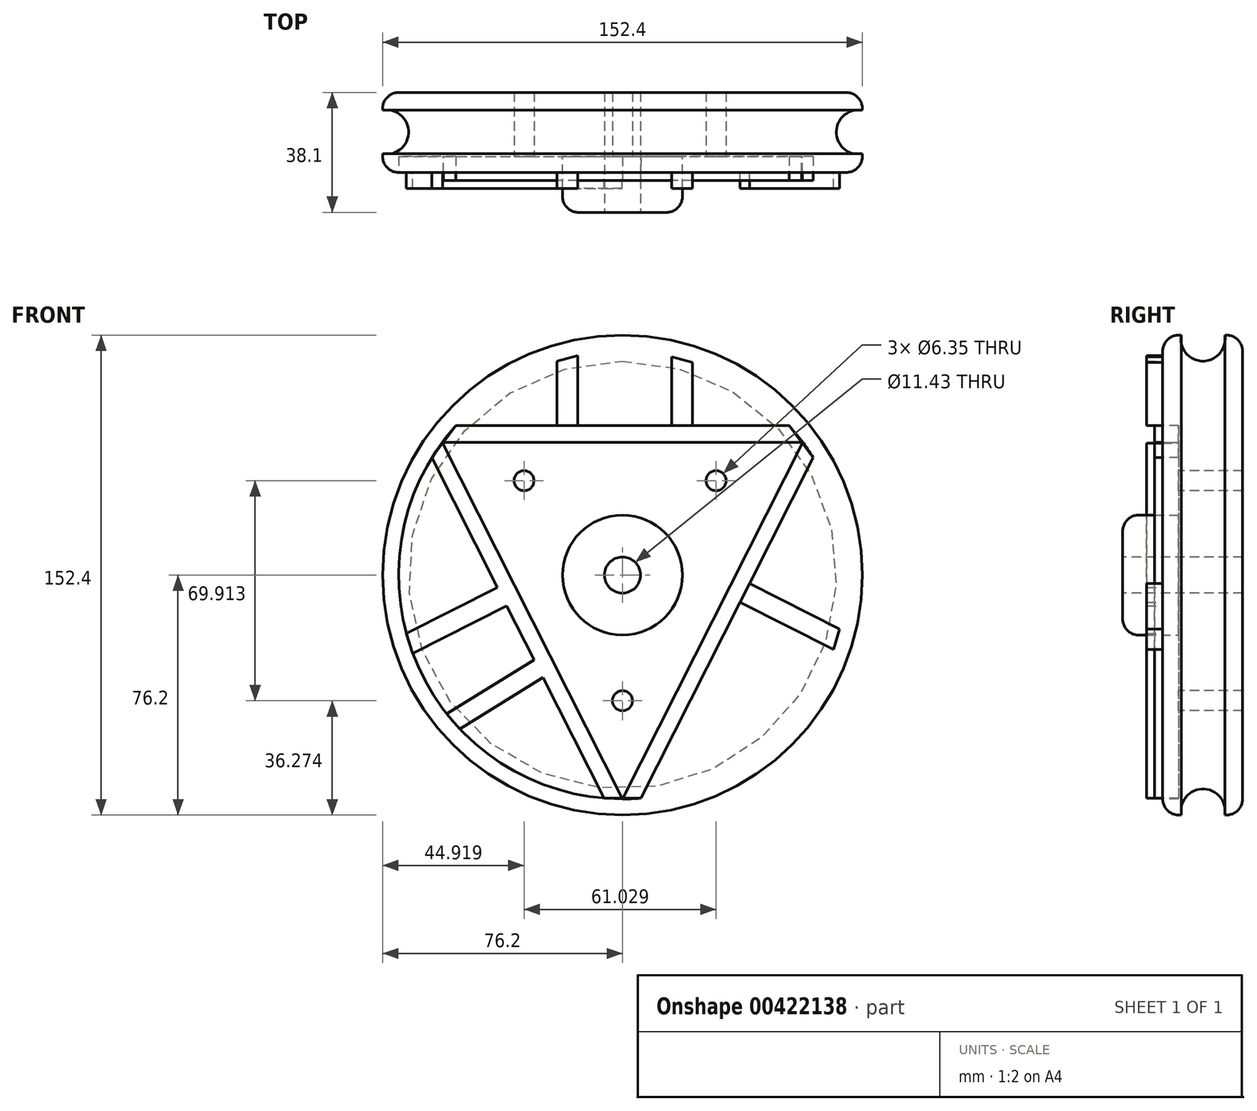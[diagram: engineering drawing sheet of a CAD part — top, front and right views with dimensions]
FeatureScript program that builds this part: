
annotation { "Feature Type Name" : "Feature", "Feature Type Description" : "" }
export const myFeature = defineFeature(function(context is Context, id is Id, definition is map)
    precondition{}
    {
        {
            var Q0;
            Q0=qCreatedBy(makeId("Front.planeOp"),FACE);
            var sketch = newSketch(context, id + "F0", { "sketchPlane" : qUnion([Q0])});
            skCircle(sketch, "E0", {"center": v(0, 0) * mm, "radius": 76.2 * mm});
            skSolve(sketch);
        }
        {
            var Q0;
            Q0=makeQuery(id+"F0.imprint","IMPRINT",FACE,{"disambiguationData":[TD([[makeQuery(id+"F0.imprint","IMPRINT",EDGE,{"derivedFrom":sQuery(id+"F0.wireOp",EDGE,"E0")}),1.0]])]});
            extrude(context, id + "F1", {"entities" : qUnion([Q0]), "depth" : 25.4 * mm, "offsetDistance" : 25.4 * mm});
        }
        {
            var Q0;
            Q0=makeQuery(id+"F1.opExtrude","CAP_FACE",FACE,{"disambiguationData":[OSD([sQuery(id+"F0.wireOp",EDGE,"E0")])],"isStart":false});
            var sketch = newSketch(context, id + "F2", { "sketchPlane" : qUnion([Q0])});
            skCircle(sketch, "E1", {"center": v(0, 0) * mm, "radius": 19.05 * mm});
            skSolve(sketch);
        }
        {
            var Q0;
            Q0=makeQuery(id+"F2.imprint","IMPRINT",FACE,{"disambiguationData":[TD([[makeQuery(id+"F2.imprint","IMPRINT",EDGE,{"derivedFrom":sQuery(id+"F2.wireOp",EDGE,"E1")}),1.0]])]});
            extrude(context, id + "F3", {"entities" : qUnion([Q0]), "operationType" : NewBodyOperationType.ADD, "depth" : 12.7 * mm, "offsetDistance" : 25.4 * mm});
        }
        {
            var Q0;
            Q0=makeQuery(id+"F1.opExtrude","CAP_EDGE",EDGE,{"disambiguationData":[OSD([sQuery(id+"F0.wireOp",EDGE,"E0")])],"isStart":false});
            var Q1;
            Q1=makeQuery(id+"F1.opExtrude","CAP_EDGE",EDGE,{"disambiguationData":[OSD([sQuery(id+"F0.wireOp",EDGE,"E0")])],"isStart":true});
            fillet(context, id + "F4", {"entities" : qUnion([Q0, Q1]), "radius" : 5.08 * mm, "tangentPropagation" : true, "allowEdgeOverflow" : false});
        }
        {
            var Q0;
            Q0=makeQuery(id+"F3.opExtrude","CAP_FACE",FACE,{"disambiguationData":[OSD([sQuery(id+"F2.wireOp",EDGE,"E1")])],"isStart":false});
            var sketch = newSketch(context, id + "F5", { "sketchPlane" : qUnion([Q0])});
            skCircle(sketch, "E2", {"center": v(0, 0) * mm, "radius": 5.72 * mm});
            skSolve(sketch);
        }
        {
            var Q0;
            Q0=makeQuery(id+"F5.imprint","IMPRINT",FACE,{"disambiguationData":[TD([[makeQuery(id+"F5.imprint","IMPRINT",EDGE,{"derivedFrom":sQuery(id+"F5.wireOp",EDGE,"E2")}),1.0]])]});
            extrude(context, id + "F6", {"entities" : qUnion([Q0]), "operationType" : NewBodyOperationType.REMOVE, "oppositeDirection" : true, "depth" : 76.2 * mm, "offsetDistance" : 25.4 * mm});
        }
        {
            var Q0;
            Q0=makeQuery(id+"F3.opExtrude","CAP_EDGE",EDGE,{"disambiguationData":[OSD([sQuery(id+"F2.wireOp",EDGE,"E1")])],"isStart":false});
            fillet(context, id + "F7", {"entities" : qUnion([Q0]), "radius" : 5.08 * mm, "tangentPropagation" : true, "allowEdgeOverflow" : false});
        }
        {
            var Q0;
            Q0=qCreatedBy(makeId("Right.planeOp"),FACE);
            var sketch = newSketch(context, id + "F8", { "sketchPlane" : qUnion([Q0])});
            skCircle(sketch, "E3", {"center": v(-12.58, 74.98) * mm, "radius": 7.03 * mm});
            skSolve(sketch);
        }
        {
            var Q0;
            Q0=makeQuery(id+"F8.imprint","IMPRINT",FACE,{"disambiguationData":[TD([[makeQuery(id+"F8.imprint","IMPRINT",EDGE,{"derivedFrom":sQuery(id+"F8.wireOp",EDGE,"E3")}),1.0]])]});
            var Q1;
            Q1=makeQuery(id+"F1.opExtrude","SWEPT_FACE",FACE,{"disambiguationData":[OSD([sQuery(id+"F0.wireOp",EDGE,"E0")])]});
            revolve(context, id + "F9", {"operationType" : NewBodyOperationType.REMOVE, "entities" : qUnion([Q0]), "axis" : qUnion([Q1]), "revolveType" : RevolveType.FULL, "oppositeDirection" : true});
        }
        {
            var Q0;
            Q0=makeQuery(id+"F1.opExtrude","CAP_FACE",FACE,{"disambiguationData":[OSD([sQuery(id+"F0.wireOp",EDGE,"E0")])],"isStart":false});
            var sketch = newSketch(context, id + "F10", { "sketchPlane" : qUnion([Q0])});
            skPoint(sketch, "E4", {"position": v(0, 44.32) * mm});
            skPoint(sketch, "E5", {"position": v(29.75, 29.99) * mm});
            skPoint(sketch, "E6", {"position": v(43.57, 0) * mm});
            skPoint(sketch, "E7", {"position": v(-31.28, 29.99) * mm});
            skPoint(sketch, "E8", {"position": v(-44.48, 0) * mm});
            skPoint(sketch, "E9", {"position": v(0, -39.93) * mm});
            skPoint(sketch, "E10", {"position": v(29.75, -26.1) * mm});
            skPoint(sketch, "E11", {"position": v(-31.28, -26.1) * mm});
            skSolve(sketch);
        }
        {
            var Q0;
            Q0=sQuery(id+"F10.wireOp",VERTEX,"E7");
            var Q1;
            Q1=sQuery(id+"F10.wireOp",VERTEX,"E9");
            var Q2;
            Q2=sQuery(id+"F10.wireOp",VERTEX,"E5");
            var Q3;
            Q3=makeQuery(id+"F1.opExtrude","SWEPT_BODY",BODY,{"disambiguationData":[OSD([sQuery(id+"F0.wireOp",EDGE,"E0")])]});
            hole(context, id + "F11", {"style" : HoleStyle.SIMPLE, "endStyle" : HoleEndStyle.THROUGH, "holeDiameter" : 6.35 * mm, "majorDiameter" : 6.35 * mm, "isTappedThrough" : true, "tappedDepth" : 12.7 * mm, "tapClearance" : 3, "locations" : qUnion([Q0, Q1, Q2]), "scope" : qUnion([Q3])});
        }
        {
            var Q0;
            Q0=makeQuery(id+"F1.opExtrude","CAP_FACE",FACE,{"disambiguationData":[OSD([sQuery(id+"F0.wireOp",EDGE,"E0")])],"isStart":false});
            var sketch = newSketch(context, id + "F12", { "sketchPlane" : qUnion([Q0])});
            skLineSegment(sketch, "E12", {"start": v(-57.28, 42.16) * mm, "end": v(57.28, 42.16) * mm});
            skLineSegment(sketch, "E13", {"start": v(57.28, 42.16) * mm, "end": v(0, -71.12) * mm});
            skLineSegment(sketch, "E14", {"start": v(0, -71.12) * mm, "end": v(-57.28, 42.16) * mm});
            skLineSegment(sketch, "E15", {"start": v(-60.57, 37.27) * mm, "end": v(-5.89, -70.88) * mm});
            skLineSegment(sketch, "E16", {"start": v(-5.89, -70.88) * mm, "end": v(5.89, -70.88) * mm});
            skLineSegment(sketch, "E17", {"start": v(5.89, -70.88) * mm, "end": v(60.57, 37.27) * mm});
            skLineSegment(sketch, "E18", {"start": v(60.57, 37.27) * mm, "end": v(52.98, 47.44) * mm});
            skLineSegment(sketch, "E19", {"start": v(52.98, 47.44) * mm, "end": v(-52.98, 47.44) * mm});
            skLineSegment(sketch, "E20", {"start": v(-52.98, 47.44) * mm, "end": v(-60.57, 37.27) * mm});
            skLineSegment(sketch, "E21", {"start": v(-36.76, -9.82) * mm, "end": v(-66.61, -24.9) * mm});
            skLineSegment(sketch, "E22", {"start": v(-66.61, -24.9) * mm, "end": v(-68.67, -18.5) * mm});
            skLineSegment(sketch, "E23", {"start": v(-68.67, -18.5) * mm, "end": v(-39.76, -3.89) * mm});
            skLineSegment(sketch, "E24", {"start": v(-39.76, -3.89) * mm, "end": v(-36.76, -9.82) * mm});
            skLineSegment(sketch, "E25", {"start": v(-25.26, -32.55) * mm, "end": v(-51.69, -48.85) * mm});
            skPoint(sketch, "E25.endSnap0", {"position": v(-51.69, -17.36) * mm});
            skLineSegment(sketch, "E26", {"start": v(-51.69, -48.85) * mm, "end": v(-55.83, -44.06) * mm});
            skLineSegment(sketch, "E27", {"start": v(-55.83, -44.06) * mm, "end": v(-28.1, -26.96) * mm});
            skLineSegment(sketch, "E28", {"start": v(-28.1, -26.96) * mm, "end": v(-25.26, -32.55) * mm});
            skLineSegment(sketch, "E29", {"start": v(25.27, -32.55) * mm, "end": v(28.1, -26.97) * mm});
            skLineSegment(sketch, "E30", {"start": v(28.1, -26.97) * mm, "end": v(25.27, -32.55) * mm});
            skLineSegment(sketch, "E31", {"start": v(53.34, -47.04) * mm, "end": v(25.27, -32.55) * mm});
            skLineSegment(sketch, "E32", {"start": v(28.1, -26.97) * mm, "end": v(57.5, -41.84) * mm});
            skLineSegment(sketch, "E33", {"start": v(57.5, -41.84) * mm, "end": v(53.34, -47.04) * mm});
            skLineSegment(sketch, "E34", {"start": v(37.36, -8.63) * mm, "end": v(67.07, -23.65) * mm});
            skLineSegment(sketch, "E35", {"start": v(67.07, -23.65) * mm, "end": v(69.01, -17.18) * mm});
            skLineSegment(sketch, "E36", {"start": v(69.01, -17.18) * mm, "end": v(40.37, -2.7) * mm});
            skLineSegment(sketch, "E37", {"start": v(40.37, -2.7) * mm, "end": v(37.36, -8.63) * mm});
            skLineSegment(sketch, "E38", {"start": v(-20.87, 47.44) * mm, "end": v(-20.87, 68) * mm});
            skLineSegment(sketch, "E39", {"start": v(-20.87, 68) * mm, "end": v(-14.21, 69.69) * mm});
            skLineSegment(sketch, "E40", {"start": v(-14.21, 69.69) * mm, "end": v(-14.21, 47.44) * mm});
            skLineSegment(sketch, "E41", {"start": v(15.58, 47.44) * mm, "end": v(15.58, 69.4) * mm});
            skLineSegment(sketch, "E42", {"start": v(15.58, 69.4) * mm, "end": v(22.24, 67.55) * mm});
            skLineSegment(sketch, "E43", {"start": v(22.24, 67.55) * mm, "end": v(22.24, 47.44) * mm});
            skSolve(sketch);
        }
        {
            var Q0;
            {var subQ5=sQuery(id+"F12.wireOp",EDGE,"E17");Q0=makeQuery(id+"F12.imprint","IMPRINT",FACE,{"disambiguationData":[TD([[makeQuery(id+"F12.imprint","IMPRINT",EDGE,{"derivedFrom":subQ5}),1.0]])]});}
            var Q1;
            {var subQ6=sQuery(id+"F12.wireOp",EDGE,"E19");Q1=makeQuery(id+"F12.imprint","IMPRINT",FACE,{"disambiguationData":[TD([[makeQuery(id+"F12.imprint","IMPRINT",EDGE,{"derivedFrom":subQ6}),1.0]])]});}
            extrude(context, id + "F13", {"entities" : qUnion([Q0, Q1]), "operationType" : NewBodyOperationType.ADD, "depth" : 2.54 * mm, "offsetDistance" : 25.4 * mm});
        }
        {
            var Q0;
            {var subQ5=sQuery(id+"F12.wireOp",EDGE,"E15");Q0=makeQuery(id+"F12.imprint","IMPRINT",FACE,{"disambiguationData":[TD([[makeQuery(id+"F12.imprint","IMPRINT",EDGE,{"derivedFrom":subQ5}),1.0]])]});}
            var Q1;
            Q1=makeQuery(id+"F12.imprint","IMPRINT",FACE,{"disambiguationData":[TD([[makeQuery(id+"F12.imprint","IMPRINT",EDGE,{"derivedFrom":sQuery(id+"F12.wireOp",EDGE,"E21")}),-1.0]])]});
            var Q2;
            Q2=makeQuery(id+"F12.imprint","IMPRINT",FACE,{"disambiguationData":[TD([[makeQuery(id+"F12.imprint","IMPRINT",EDGE,{"derivedFrom":sQuery(id+"F12.wireOp",EDGE,"1ifUW7IA-ng5w-8Yun-7v0P-wnSl1J1wXTwM")}),1.0]])]});
            var Q3;
            Q3=makeQuery(id+"F12.imprint","IMPRINT",FACE,{"disambiguationData":[TD([[makeQuery(id+"F12.imprint","IMPRINT",EDGE,{"derivedFrom":sQuery(id+"F12.wireOp",EDGE,"4Hk6yBfX-HIW3-ntNp-zyZ5-2kZEGo1H1oCN.bottom")}),1.0]])]});
            var Q4;
            Q4=makeQuery(id+"F12.imprint","IMPRINT",FACE,{"disambiguationData":[TD([[makeQuery(id+"F12.imprint","IMPRINT",EDGE,{"derivedFrom":sQuery(id+"F12.wireOp",EDGE,"aM3cGKz6-Hocq-mmRq-TTYN-cNw8dTAOU88D")}),-1.0]])]});
            var Q5;
            Q5=makeQuery(id+"F12.imprint","IMPRINT",FACE,{"disambiguationData":[TD([[makeQuery(id+"F12.imprint","IMPRINT",EDGE,{"derivedFrom":sQuery(id+"F12.wireOp",EDGE,"aM3cGKz6-Hocq-mmRq-TTYN-cNw8dTAOU88D")}),-1.0]])]});
            var Q6;
            Q6=makeQuery(id+"F12.imprint","IMPRINT",FACE,{"disambiguationData":[TD([[makeQuery(id+"F12.imprint","IMPRINT",EDGE,{"derivedFrom":sQuery(id+"F12.wireOp",EDGE,"E25")}),-1.0]])]});
            var Q7;
            Q7=makeQuery(id+"F12.imprint","IMPRINT",FACE,{"disambiguationData":[TD([[makeQuery(id+"F12.imprint","IMPRINT",EDGE,{"derivedFrom":sQuery(id+"F12.wireOp",EDGE,"E30")}),1.0]])]});
            var Q8;
            Q8=makeQuery(id+"F12.imprint","IMPRINT",FACE,{"disambiguationData":[TD([[makeQuery(id+"F12.imprint","IMPRINT",EDGE,{"derivedFrom":sQuery(id+"F12.wireOp",EDGE,"E34")}),1.0]])]});
            var Q9;
            {var subQ0=sQuery(id+"F12.wireOp",EDGE,"E41");Q9=makeQuery(id+"F12.imprint","IMPRINT",FACE,{"disambiguationData":[TD([[makeQuery(id+"F12.imprint","IMPRINT",EDGE,{"derivedFrom":subQ0}),-1.0]])]});}
            var Q10;
            {var subQ0=sQuery(id+"F12.wireOp",EDGE,"E38");Q10=makeQuery(id+"F12.imprint","IMPRINT",FACE,{"disambiguationData":[TD([[makeQuery(id+"F12.imprint","IMPRINT",EDGE,{"derivedFrom":subQ0}),-1.0]])]});}
            extrude(context, id + "F14", {"entities" : qUnion([Q0, Q1, Q2, Q3, Q4, Q5, Q6, Q7, Q8, Q9, Q10]), "depth" : 5.08 * mm, "offsetDistance" : 25.4 * mm});
        }
        {
            var Q0;
            {var subQ0=sQuery(id+"F12.wireOp",EDGE,"E17");var subQ1=sQuery(id+"F12.wireOp",EDGE,"E13");var subQ2=sQuery(id+"F12.wireOp",EDGE,"E12");var subQ3=sQuery(id+"F0.wireOp",EDGE,"E0");var subQ4=makeQuery(id+"F1.opExtrude","CAP_FACE",FACE,{"disambiguationData":[OSD([subQ3])],"isStart":false});var subQ5=sQuery(id+"F12.wireOp",EDGE,"E19");var subQ6=makeQuery(id+"F1.opExtrude","CAP_EDGE",EDGE,{"disambiguationData":[OSD([subQ3])],"isStart":false});var subQ7=sQuery(id+"F12.wireOp",EDGE,"E18");var subQ8=subQ4;Q0=makeQuery(id+"F13.boolean.opBoolean","SPLIT",FACE,{"disambiguationData":[TD([subQ4,makeQuery(id+"F3.opExtrude","SWEPT_FACE",FACE,{"disambiguationData":[OSD([sQuery(id+"F2.wireOp",EDGE,"E1")])]}),makeQuery(id+"F4.opFillet","BLEND_FACE",FACE,{"disambiguationData":[OSD([subQ3]),TDD([subQ6])]}),makeQuery(id+"F11.hole-0.boolean.opBoolean","COPY",FACE,{"derivedFrom":makeQuery(id+"F11.hole-0.opRevolve","SWEPT_FACE",FACE,{"disambiguationData":[OSD([sQuery(id+"F11.hole-0.sketch.wireOp",EDGE,"core_line_2")])]})}),makeQuery(id+"F11.hole-1.boolean.opBoolean","COPY",FACE,{"derivedFrom":makeQuery(id+"F11.hole-1.opRevolve","SWEPT_FACE",FACE,{"disambiguationData":[OSD([sQuery(id+"F11.hole-1.sketch.wireOp",EDGE,"core_line_2")])]})}),makeQuery(id+"F11.hole-2.boolean.opBoolean","COPY",FACE,{"derivedFrom":makeQuery(id+"F11.hole-2.opRevolve","SWEPT_FACE",FACE,{"disambiguationData":[OSD([sQuery(id+"F11.hole-2.sketch.wireOp",EDGE,"core_line_2")])]})}),makeQuery(id+"F13.opExtrude","SWEPT_FACE",FACE,{"disambiguationData":[OSD([subQ2])]}),makeQuery(id+"F13.opExtrude","SWEPT_FACE",FACE,{"disambiguationData":[OSD([subQ1])]}),makeQuery(id+"F13.opExtrude","SWEPT_FACE",FACE,{"disambiguationData":[OSD([sQuery(id+"F12.wireOp",EDGE,"E16")])]}),makeQuery(id+"F13.opExtrude","SWEPT_FACE",FACE,{"disambiguationData":[OSD([subQ0,sQuery(id+"F12.wireOp",EDGE,"E30"),sQuery(id+"F12.wireOp",EDGE,"E37")])]}),makeQuery(id+"F13.opExtrude","SWEPT_FACE",FACE,{"disambiguationData":[OSD([subQ7]),TDD([makeQuery(id+"F12.imprint","IMPRINT",EDGE,{"disambiguationData":[TD([[makeQuery(id+"F12.imprint","INTERSECT",VERTEX,{"derivedFrom":[subQ1,subQ7]}),1.0]])],"derivedFrom":subQ7})])]}),makeQuery(id+"F13.opExtrude","SWEPT_FACE",FACE,{"disambiguationData":[OSD([subQ7]),TDD([makeQuery(id+"F12.imprint","IMPRINT",EDGE,{"disambiguationData":[TD([[makeQuery(id+"F12.imprint","INTERSECT",VERTEX,{"derivedFrom":[subQ2,subQ7]}),-1.0]])],"derivedFrom":subQ7})])]}),makeQuery(id+"F13.opExtrude","SWEPT_FACE",FACE,{"disambiguationData":[OSD([subQ5])]}),makeQuery(id+"F13.opExtrude","SWEPT_FACE",FACE,{"disambiguationData":[OSD([sQuery(id+"F12.wireOp",EDGE,"E20")])]})])],"derivedFrom":subQ8});}
            var sketch = newSketch(context, id + "F15", { "sketchPlane" : qUnion([Q0])});
            skLineSegment(sketch, "E44", {"start": v(-44.81, 34.64) * mm, "end": v(46.62, 34.64) * mm});
            skLineSegment(sketch, "E45", {"start": v(46.62, 34.64) * mm, "end": v(0, -53.98) * mm});
            skLineSegment(sketch, "E46", {"start": v(54.12, 42.16) * mm, "end": v(46.62, 42.16) * mm});
            skLineSegment(sketch, "E47", {"start": v(-1.92, -67.32) * mm, "end": v(0.12, -70.88) * mm});
            skLineSegment(sketch, "E48", {"start": v(0.12, -70.88) * mm, "end": v(2, -67.32) * mm});
            skLineSegment(sketch, "E49", {"start": v(2, -50.19) * mm, "end": v(-1.92, -50.18) * mm});
            skLineSegment(sketch, "E50.bottom", {"start": v(-1.92, -50.18) * mm, "end": v(2, -50.18) * mm});
            skLineSegment(sketch, "E50.top", {"start": v(-1.92, -67.32) * mm, "end": v(2, -67.32) * mm});
            skLineSegment(sketch, "E51", {"start": v(-44.75, 42.16) * mm, "end": v(-36.7, 34.64) * mm});
            skLineSegment(sketch, "E52", {"start": v(-44.81, 34.64) * mm, "end": v(0, -53.98) * mm});
            skSolve(sketch);
        }
        {
            var Q0;
            {var subQ0=sQuery(id+"F15.wireOp",EDGE,"TjXxPUKX-lexW-nX49-w7Sp-vmFD8uqPiQYd");Q0=makeQuery(id+"F15.imprint","IMPRINT",FACE,{"disambiguationData":[TD([[makeQuery(id+"F15.imprint","IMPRINT",EDGE,{"derivedFrom":subQ0}),-1.0]])]});}
            var Q1;
            {var subQ0=sQuery(id+"F15.wireOp",EDGE,"xPqLRQk2-zaOM-Hrsm-gSkG-elz6mGtjtou3");Q1=makeQuery(id+"F15.imprint","IMPRINT",FACE,{"disambiguationData":[TD([[makeQuery(id+"F15.imprint","IMPRINT",EDGE,{"derivedFrom":subQ0}),1.0]])]});}
            var Q2;
            {var subQ0=sQuery(id+"F15.wireOp",EDGE,"9i8OcQG0-GGTl-4JnO-ULQ2-bq8hi4Ufm7qi");Q2=makeQuery(id+"F15.imprint","IMPRINT",FACE,{"disambiguationData":[TD([[makeQuery(id+"F15.imprint","IMPRINT",EDGE,{"derivedFrom":subQ0}),1.0]])]});}
            var Q3;
            {var subQ3=sQuery(id+"F15.wireOp",EDGE,"E49");Q3=makeQuery(id+"F15.imprint","IMPRINT",FACE,{"disambiguationData":[TD([[makeQuery(id+"F15.imprint","IMPRINT",EDGE,{"derivedFrom":subQ3}),-1.0]])]});}
            var Q4;
            Q4=sQuery(id+"F15.wireOp",EDGE,"E45");
            var Q5;
            Q5=sQuery(id+"F15.wireOp",EDGE,"E52");
            var Q6;
            Q6=sQuery(id+"F15.wireOp",EDGE,"E44");
            extrude(context, id + "F16", {"entities" : qUnion([Q0, Q1, Q2, Q3]), "bodyType" : ToolBodyType.SURFACE, "surfaceEntities" : qUnion([Q4, Q5, Q6]), "depth" : 6.35 * mm, "offsetDistance" : 25.4 * mm});
        }
        {
            var Q0;
            {var subQ0=sQuery(id+"F12.wireOp",EDGE,"E17");var subQ1=sQuery(id+"F12.wireOp",EDGE,"E13");var subQ2=sQuery(id+"F12.wireOp",EDGE,"E12");var subQ3=sQuery(id+"F0.wireOp",EDGE,"E0");var subQ4=makeQuery(id+"F1.opExtrude","CAP_FACE",FACE,{"disambiguationData":[OSD([subQ3])],"isStart":false});var subQ5=sQuery(id+"F12.wireOp",EDGE,"E19");var subQ6=makeQuery(id+"F1.opExtrude","CAP_EDGE",EDGE,{"disambiguationData":[OSD([subQ3])],"isStart":false});var subQ7=sQuery(id+"F12.wireOp",EDGE,"E18");var subQ8=subQ4;Q0=makeQuery(id+"F13.boolean.opBoolean","SPLIT",FACE,{"disambiguationData":[TD([subQ4,makeQuery(id+"F3.opExtrude","SWEPT_FACE",FACE,{"disambiguationData":[OSD([sQuery(id+"F2.wireOp",EDGE,"E1")])]}),makeQuery(id+"F4.opFillet","BLEND_FACE",FACE,{"disambiguationData":[OSD([subQ3]),TDD([subQ6])]}),makeQuery(id+"F11.hole-0.boolean.opBoolean","COPY",FACE,{"derivedFrom":makeQuery(id+"F11.hole-0.opRevolve","SWEPT_FACE",FACE,{"disambiguationData":[OSD([sQuery(id+"F11.hole-0.sketch.wireOp",EDGE,"core_line_2")])]})}),makeQuery(id+"F11.hole-1.boolean.opBoolean","COPY",FACE,{"derivedFrom":makeQuery(id+"F11.hole-1.opRevolve","SWEPT_FACE",FACE,{"disambiguationData":[OSD([sQuery(id+"F11.hole-1.sketch.wireOp",EDGE,"core_line_2")])]})}),makeQuery(id+"F11.hole-2.boolean.opBoolean","COPY",FACE,{"derivedFrom":makeQuery(id+"F11.hole-2.opRevolve","SWEPT_FACE",FACE,{"disambiguationData":[OSD([sQuery(id+"F11.hole-2.sketch.wireOp",EDGE,"core_line_2")])]})}),makeQuery(id+"F13.opExtrude","SWEPT_FACE",FACE,{"disambiguationData":[OSD([subQ2])]}),makeQuery(id+"F13.opExtrude","SWEPT_FACE",FACE,{"disambiguationData":[OSD([subQ1])]}),makeQuery(id+"F13.opExtrude","SWEPT_FACE",FACE,{"disambiguationData":[OSD([sQuery(id+"F12.wireOp",EDGE,"E16")])]}),makeQuery(id+"F13.opExtrude","SWEPT_FACE",FACE,{"disambiguationData":[OSD([subQ0,sQuery(id+"F12.wireOp",EDGE,"E30"),sQuery(id+"F12.wireOp",EDGE,"E37")])]}),makeQuery(id+"F13.opExtrude","SWEPT_FACE",FACE,{"disambiguationData":[OSD([subQ7]),TDD([makeQuery(id+"F12.imprint","IMPRINT",EDGE,{"disambiguationData":[TD([[makeQuery(id+"F12.imprint","INTERSECT",VERTEX,{"derivedFrom":[subQ1,subQ7]}),1.0]])],"derivedFrom":subQ7})])]}),makeQuery(id+"F13.opExtrude","SWEPT_FACE",FACE,{"disambiguationData":[OSD([subQ7]),TDD([makeQuery(id+"F12.imprint","IMPRINT",EDGE,{"disambiguationData":[TD([[makeQuery(id+"F12.imprint","INTERSECT",VERTEX,{"derivedFrom":[subQ2,subQ7]}),-1.0]])],"derivedFrom":subQ7})])]}),makeQuery(id+"F13.opExtrude","SWEPT_FACE",FACE,{"disambiguationData":[OSD([subQ5])]}),makeQuery(id+"F13.opExtrude","SWEPT_FACE",FACE,{"disambiguationData":[OSD([sQuery(id+"F12.wireOp",EDGE,"E20")])]})])],"derivedFrom":subQ8});}
            extrude(context, id + "F17", {"entities" : qUnion([Q0]), "operationType" : NewBodyOperationType.REMOVE, "oppositeDirection" : true, "depth" : 5.08 * mm, "offsetDistance" : 25.4 * mm});
        }
    });
